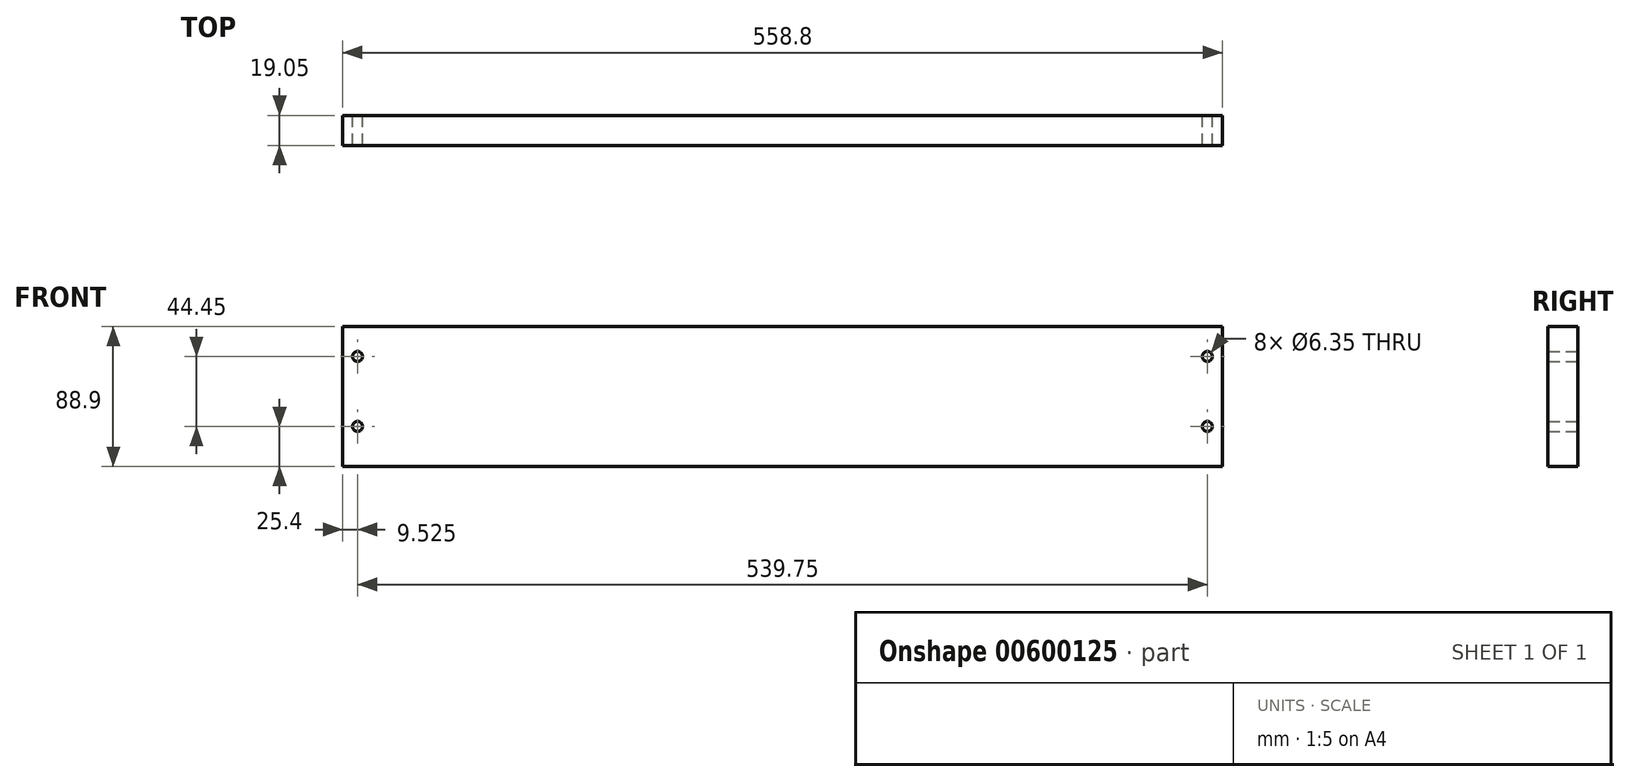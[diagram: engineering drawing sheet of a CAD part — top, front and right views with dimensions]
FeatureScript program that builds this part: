
annotation { "Feature Type Name" : "Feature", "Feature Type Description" : "" }
export const myFeature = defineFeature(function(context is Context, id is Id, definition is map)
    precondition{}
    {
        {
            var Q0;
            Q0=qCreatedBy(makeId("Front.planeOp"),FACE);
            var sketch = newSketch(context, id + "F0", { "sketchPlane" : qUnion([Q0])});
            skLineSegment(sketch, "E0.bottom", {"start": v(0, 0) * mm, "end": v(-558.8, 0) * mm});
            skLineSegment(sketch, "E0.top", {"start": v(0, 88.9) * mm, "end": v(-558.8, 88.9) * mm});
            skLineSegment(sketch, "E0.left", {"start": v(0, 0) * mm, "end": v(0, 88.9) * mm});
            skLineSegment(sketch, "E0.right", {"start": v(-558.8, 0) * mm, "end": v(-558.8, 88.9) * mm});
            skLineSegment(sketch, "E1", {"start": v(-539.75, 88.9) * mm, "end": v(-539.75, 6.35) * mm, "construction": true});
            skLineSegment(sketch, "E2", {"start": v(-539.75, 6.35) * mm, "end": v(-558.8, 6.35) * mm, "construction": true});
            skLineSegment(sketch, "E3", {"start": v(-549.28, 6.35) * mm, "end": v(-549.28, 25.4) * mm, "construction": true});
            skLineSegment(sketch, "E4", {"start": v(-549.28, 25.4) * mm, "end": v(-549.28, 69.85) * mm, "construction": true});
            skCircle(sketch, "E5", {"center": v(-549.28, 69.85) * mm, "radius": 3.18 * mm});
            skCircle(sketch, "E6", {"center": v(-549.28, 25.4) * mm, "radius": 3.18 * mm});
            skLineSegment(sketch, "E7", {"start": v(-279.4, 0) * mm, "end": v(-279.4, 65) * mm, "construction": true});
            skPoint(sketch, "E7.endSnap0", {"position": v(-279.4, 0) * mm});
            skCircle(sketch, "E8.MirrorC", {"center": v(-9.53, 69.85) * mm, "radius": 3.18 * mm});
            skCircle(sketch, "E9.MirrorC", {"center": v(-9.53, 25.4) * mm, "radius": 3.18 * mm});
            skSolve(sketch);
        }
        {
            var Q0;
            Q0=qSketchRegion(id+"F0",true);
            extrude(context, id + "F1", {"entities" : qUnion([Q0]), "depth" : 19.05 * mm, "offsetDistance" : 25.4 * mm});
        }
    });
